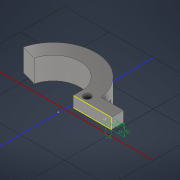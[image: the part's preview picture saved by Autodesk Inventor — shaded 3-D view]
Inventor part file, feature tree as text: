
AUTODESK INVENTOR PART (.ipt)
format: ipt  version: 2021 (Build 250183000, 183)  size: 163,328 bytes
history: native  units: mm
features: sketch x6, extrude x4, projected_geometry x2, plane x1, split x1, hole x1, fillet x1
ambient origin geometry x8: Origin, YZ Plane, XZ Plane, XY Plane, X Axis, Y Axis, Z Axis, Center Point
bodies: Solid1 (feature_tree)
feature tree (16):
  extrude  "Extrusion1"  Depth=12.0mm
  plane  "Work Plane1"
  split  "Split1"
  extrude  "Extrusion2"  TaperAngle=0.0deg  [1 undecoded]
  extrude  "Extrusion3"  TaperAngle=0.0deg  [1 undecoded]
  hole  "Hole1"  [1 undecoded]
  extrude  "halfCut"  Depth=10.0mm TaperAngle=0.0deg
  fillet  "Fillet1"  Radius=10.0mm
  sketch  "Sketch6"  dims[d15=0.0mm d16=3.559644mm d17=7.119287mm d18=3.25mm d19=6.0mm d20=4.0mm d21=2.0mm d22=90.0deg d23=8.0mm d24=20.594885mm d26=5.5mm d27=0.0mm d28=1.0mm d29=5.25mm d30=6.5mm d31=20.0mm d32=0.0mm d33=2.375mm d34=4.75mm d35=2.5mm]
  sketch  "Sketch1"  dims[d0=12.0mm d2=3.0mm]
  sketch  "Sketch2"  dims[d3=12.0mm d4=0.0mm]
  projected_geometry  "Projected Loop1"
  sketch  "Sketch3"  dims[d5=5.0mm d6=0.0mm]
  projected_geometry  "Projected Loop2"
  sketch  "Sketch4"  dims[d7=7.0mm d8=10.0mm d9=0.0mm]
  sketch  "Sketch5"  dims[d10=-2.75mm d11=5.5mm d12=0.0mm d13=10.0mm d14=0.0mm]
note: 3 required parameter values undecoded (feature->parameter linkage not recoverable at this tier; creation-order binding heuristic only, values carry confidence <= 0.55)
